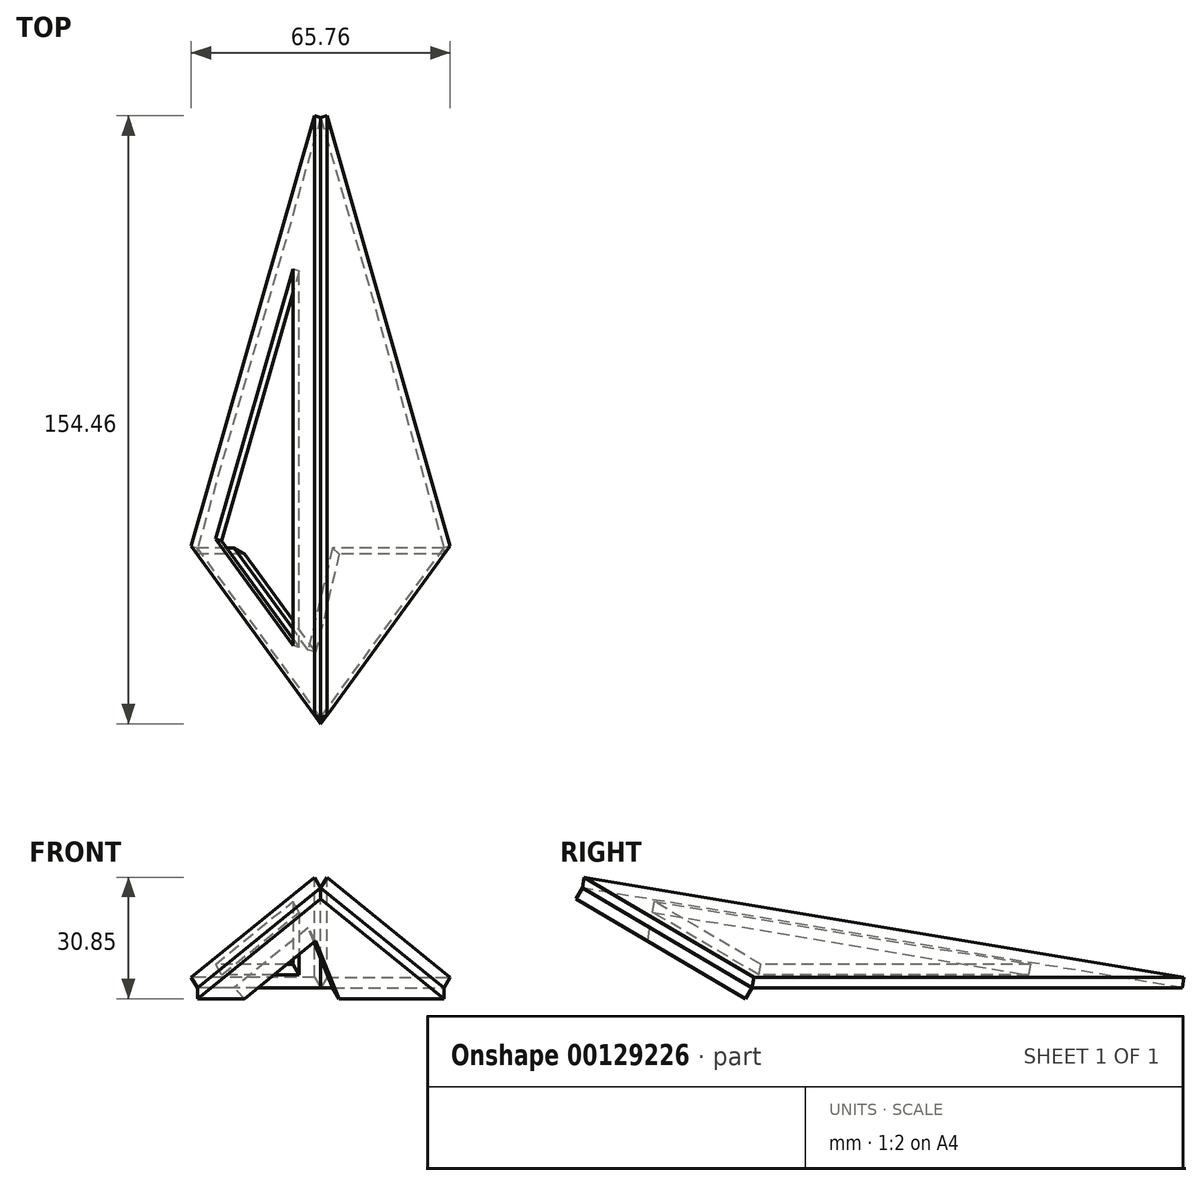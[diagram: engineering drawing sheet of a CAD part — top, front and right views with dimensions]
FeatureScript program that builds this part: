
annotation { "Feature Type Name" : "Feature", "Feature Type Description" : "" }
export const myFeature = defineFeature(function(context is Context, id is Id, definition is map)
    precondition{}
    {
        {
            var Q0;
            Q0=qCreatedBy(makeId("Top.planeOp"),FACE);
            var sketch = newSketch(context, id + "F0", { "sketchPlane" : qUnion([Q0])});
            skLineSegment(sketch, "E0", {"start": v(0, 152.4) * mm, "end": v(-31.3, 43.07) * mm});
            skLineSegment(sketch, "E1", {"start": v(-31.3, 43.07) * mm, "end": v(0, 0) * mm});
            skLineSegment(sketch, "E2.MirrorCS", {"start": v(0, 152.4) * mm, "end": v(31.3, 43.07) * mm});
            skLineSegment(sketch, "E3.MirrorCS", {"start": v(31.3, 43.07) * mm, "end": v(0, 0) * mm});
            skLineSegment(sketch, "E4", {"start": v(0, 152.4) * mm, "end": v(0, 0) * mm});
            skLineSegment(sketch, "E5.1.1", {"start": v(-50.64, -16.45) * mm, "end": v(0, 0) * mm});
            skLineSegment(sketch, "E5.1.2", {"start": v(-144.94, 47.1) * mm, "end": v(-50.64, -16.45) * mm});
            skLineSegment(sketch, "E5.1.3", {"start": v(-144.94, 47.1) * mm, "end": v(0, 0) * mm});
            skLineSegment(sketch, "E5.1.4", {"start": v(-144.94, 47.1) * mm, "end": v(-31.3, 43.07) * mm});
            skLineSegment(sketch, "E5.2.0", {"start": v(-50.64, -16.45) * mm, "end": v(0, 0) * mm});
            skLineSegment(sketch, "E5.2.1", {"start": v(0, -53.24) * mm, "end": v(0, 0) * mm});
            skLineSegment(sketch, "E5.2.2", {"start": v(-89.58, -123.3) * mm, "end": v(0, -53.24) * mm});
            skLineSegment(sketch, "E5.2.3", {"start": v(-89.58, -123.3) * mm, "end": v(0, 0) * mm});
            skLineSegment(sketch, "E5.2.4", {"start": v(-89.58, -123.3) * mm, "end": v(-50.64, -16.45) * mm});
            skLineSegment(sketch, "E5.3.0", {"start": v(0, -53.24) * mm, "end": v(0, 0) * mm});
            skLineSegment(sketch, "E5.3.1", {"start": v(50.64, -16.45) * mm, "end": v(0, 0) * mm});
            skLineSegment(sketch, "E5.3.2", {"start": v(89.58, -123.3) * mm, "end": v(50.64, -16.45) * mm});
            skLineSegment(sketch, "E5.3.3", {"start": v(89.58, -123.3) * mm, "end": v(0, 0) * mm});
            skLineSegment(sketch, "E5.3.4", {"start": v(89.58, -123.3) * mm, "end": v(0, -53.24) * mm});
            skLineSegment(sketch, "E5.4.0", {"start": v(50.64, -16.45) * mm, "end": v(0, 0) * mm});
            skLineSegment(sketch, "E5.4.2", {"start": v(144.94, 47.1) * mm, "end": v(31.3, 43.07) * mm});
            skLineSegment(sketch, "E5.4.3", {"start": v(144.94, 47.1) * mm, "end": v(0, 0) * mm});
            skLineSegment(sketch, "E5.4.4", {"start": v(144.94, 47.1) * mm, "end": v(50.64, -16.45) * mm});
            skPoint(sketch, "E5.center", {"position": v(0, 0) * mm});
            skLineSegment(sketch, "E6", {"start": v(-31.3, 43.07) * mm, "end": v(31.3, 43.07) * mm, "construction": true});
            skSolve(sketch);
        }
        {
            var Q0;
            Q0=qCreatedBy(makeId("Right.planeOp"),FACE);
            var sketch = newSketch(context, id + "F1", { "sketchPlane" : qUnion([Q0])});
            skPoint(sketch, "E7.0", {"position": v(152.4, 0) * mm});
            skPoint(sketch, "E7.1", {"position": v(0, 0) * mm});
            skLineSegment(sketch, "E8", {"start": v(152.4, 0) * mm, "end": v(0, 25.4) * mm});
            skLineSegment(sketch, "E9", {"start": v(0, 25.4) * mm, "end": v(0, 0) * mm});
            skSolve(sketch);
        }
        {
            var Q0;
            Q0=sQuery(id+"F0.wireOp",EDGE,"E3.MirrorCS");
            var Q1;
            Q1=sQuery(id+"F1.wireOp",EDGE,"E9");
            cPlane(context, id + "F2", {"entities" : qUnion([Q0, Q1]), "cplaneType" : CPlaneType.LINE_ANGLE, "offset" : 25.4 * mm, "angle" : 0 * degree, "width" : 152.4 * mm, "height" : 152.4 * mm});
        }
        {
            var Q0;
            Q0=qCreatedBy(id+"F2.planeOp",FACE);
            var sketch = newSketch(context, id + "F3", { "sketchPlane" : qUnion([Q0])});
            skPoint(sketch, "E10.0", {"position": v(53.24, 0) * mm});
            skPoint(sketch, "E10.1", {"position": v(0, 25.4) * mm});
            skLineSegment(sketch, "E11", {"start": v(0, 25.4) * mm, "end": v(53.24, 0) * mm});
            skSolve(sketch);
        }
        {
            var Q0;
            Q0=sQuery(id+"F0.wireOp",EDGE,"E2.MirrorCS");
            var Q1;
            Q1=sQuery(id+"F3.wireOp",EDGE,"E11");
            cPlane(context, id + "F4", {"entities" : qUnion([Q0, Q1]), "cplaneType" : CPlaneType.LINE_ANGLE, "offset" : 25.4 * mm, "angle" : 0 * degree, "width" : 152.4 * mm, "height" : 152.4 * mm});
        }
        {
            var Q0;
            Q0=qCreatedBy(id+"F4.planeOp",FACE);
            var sketch = newSketch(context, id + "F5", { "sketchPlane" : qUnion([Q0])});
            skLineSegment(sketch, "E12.0", {"start": v(-12.48, 150.33) * mm, "end": v(23.61, 42.49) * mm});
            skLineSegment(sketch, "E12.1", {"start": v(-12.48, 150.33) * mm, "end": v(-12.48, -4.18) * mm});
            skLineSegment(sketch, "E12.2", {"start": v(-12.48, -4.18) * mm, "end": v(23.61, 42.49) * mm});
            skSolve(sketch);
        }
        {
            var Q0;
            Q0 = qSketchRegion(id + "F5", true);
            extrude(context, id + "F6", {"entities" : qUnion([Q0]), "depth" : 3.17 * mm});
        }
        {
            var Q0;
            Q0=makeQuery(id+"F6.opExtrude","SWEPT_BODY",BODY,{"disambiguationData":[OSD([sQuery(id+"F5.wireOp",EDGE,"E12.0"),sQuery(id+"F5.wireOp",EDGE,"E12.1"),sQuery(id+"F5.wireOp",EDGE,"E12.2")])]});
            var Q1;
            Q1=qCreatedBy(makeId("Right.planeOp"),FACE);
            mirror(context, id + "F7", {"entities" : qUnion([Q0]), "mirrorPlane" : qUnion([Q1])});
        }
        {
            var Q0;
            Q0=sQuery(id+"F0.wireOp",EDGE,"E6");
            var Q1;
            Q1=makeQuery(id+"F6.opExtrude","CAP_VERTEX",VERTEX,{"disambiguationData":[OSD([sQuery(id+"F5.wireOp",EDGE,"E12.1"),sQuery(id+"F5.wireOp",EDGE,"E12.2")])],"isStart":true});
            cPlane(context, id + "F8", {"entities" : qUnion([Q0, Q1]), "cplaneType" : CPlaneType.LINE_ANGLE, "offset" : 25.4 * mm, "angle" : 0 * degree, "width" : 152.4 * mm, "height" : 152.4 * mm});
        }
        {
            var Q0;
            Q0=qCreatedBy(id+"F8.planeOp",FACE);
            var sketch = newSketch(context, id + "F9", { "sketchPlane" : qUnion([Q0])});
            skLineSegment(sketch, "E13", {"start": v(31.3, -37.1) * mm, "end": v(0, 12.9) * mm});
            skLineSegment(sketch, "E14", {"start": v(0, 12.9) * mm, "end": v(-31.3, -37.1) * mm});
            skLineSegment(sketch, "E15", {"start": v(0, -37.1) * mm, "end": v(-31.3, -37.1) * mm});
            skLineSegment(sketch, "E16", {"start": v(31.3, -37.1) * mm, "end": v(0, -37.1) * mm});
            skSolve(sketch);
        }
        {
            var Q0;
            Q0 = qSketchRegion(id + "F9", true);
            extrude(context, id + "F10", {"entities" : qUnion([Q0]), "depth" : 3.17 * mm});
        }
        {
            var Q0;
            Q0=makeQuery(id+"F7.opPattern","COPY",FACE,{"derivedFrom":makeQuery(id+"F6.opExtrude","CAP_FACE",FACE,{"disambiguationData":[OSD([sQuery(id+"F5.wireOp",EDGE,"E12.0"),sQuery(id+"F5.wireOp",EDGE,"E12.1"),sQuery(id+"F5.wireOp",EDGE,"E12.2")])],"isStart":false}),"instanceName":"1"});
            var sketch = newSketch(context, id + "F11", { "sketchPlane" : qUnion([Q0])});
            skLineSegment(sketch, "E17.0.0", {"start": v(12.48, 150.33) * mm, "end": v(-23.61, 42.49) * mm});
            skLineSegment(sketch, "E17.0.1", {"start": v(-23.61, 42.49) * mm, "end": v(12.48, -4.18) * mm});
            skLineSegment(sketch, "E17.0.2", {"start": v(12.48, -4.18) * mm, "end": v(12.48, 150.33) * mm});
            skLineSegment(sketch, "E18.0", {"start": v(6.13, 111.34) * mm, "end": v(-16.51, 43.69) * mm});
            skLineSegment(sketch, "E18.1", {"start": v(6.13, 14.41) * mm, "end": v(6.13, 111.34) * mm});
            skLineSegment(sketch, "E18.2", {"start": v(-16.51, 43.69) * mm, "end": v(6.13, 14.41) * mm});
            skSolve(sketch);
        }
        {
            var Q0;
            Q0=makeQuery(id+"F11.imprint","IMPRINT",FACE,{"disambiguationData":[TD([[makeQuery(id+"F11.imprint","IMPRINT",EDGE,{"derivedFrom":sQuery(id+"F11.wireOp",EDGE,"E18.0")}),1.0]])]});
            extrude(context, id + "F12", {"entities" : qUnion([Q0]), "operationType" : NewBodyOperationType.REMOVE, "endBound" : BoundingType.THROUGH_ALL, "oppositeDirection" : true, "depth" : 25.4 * mm});
        }
    });
